# Revit family: EKF_EE_ЩИТCrosser_IP31_PROxima
name_source: partatom
category: Электрооборудование
units: mm (PartAtom-declared; Revit-internal decimal feet)

## family parameters
Всегда вертикально = Да
На основе рабочей плоскости = Нет
Общий = Нет
При загрузке вырезать с полостями = Нет
Размер круглого соединителя = Использовать диаметр
Тип детали = Другая панель
Точка расчета площади = Да

## types (3) — shared parameters
ADSK_Единица измерения = компл.
ADSK_Завод-изготовитель = EKF
ADSK_Классификация нагрузок = Прочее
ADSK_Количество = 1
ADSK_Коэффициент мощности = 1
ADSK_Марка = Щит
ADSK_Материал = RAL 9001
ADSK_Номинальная мощность = 0 Вт
ADSK_Обозначение = Щит
ADSK_Полная мощность = 0 В·А
ADSK_Размер_Глубина = 120 мм
ADSK_Размер_Ширина = 340 мм
ADSK_Ток = 0 А
Изготовитель = EKF
Комплект = 1. Металлокорпус с монтажной панелью – 1 шт. 2. Поводок заземления – 1 шт. 3. Замок IP31 – 1 шт. 4. Знаки электробезопасности. 5. Монтажный комплект – 1 шт. 6. Паспорт – 1 шт.
Серия номенклатуры = PROxima
Степень защиты IP = IP31
ТВ = EKF_2
Тип установки = Встраиваемый
zero-valued in all types: Количество DIN-реек, Количество модулей на DIN-рейке, Максимальное количество модулей

## per-type parameters (varying)
| type | ADSK_Код изделия | ADSK_Количество фаз | ADSK_Масса | ADSK_Напряжение | ADSK_Размер_Высота | Тип |
| Щит Crosser R-1 (390х340х120) IP31 EKF PROxima | c-r-1 | 1 | 3.9 | 0 В | 390 мм | 1 мм |
| Щит Crosser R-2 (520х340х120) IP31 EKF PROxima | c-r-2 | 3 | 5.1 | 400 В | 520 мм | 2 мм |
| Щит Crosser R-3 (650х340х120) IP31 EKF PROxima | c-r-3 | 3 | 6.6 | 400 В | 650 мм | 3 мм |

note: column(s) folded — value = type name in every type: ADSK_Наименование
